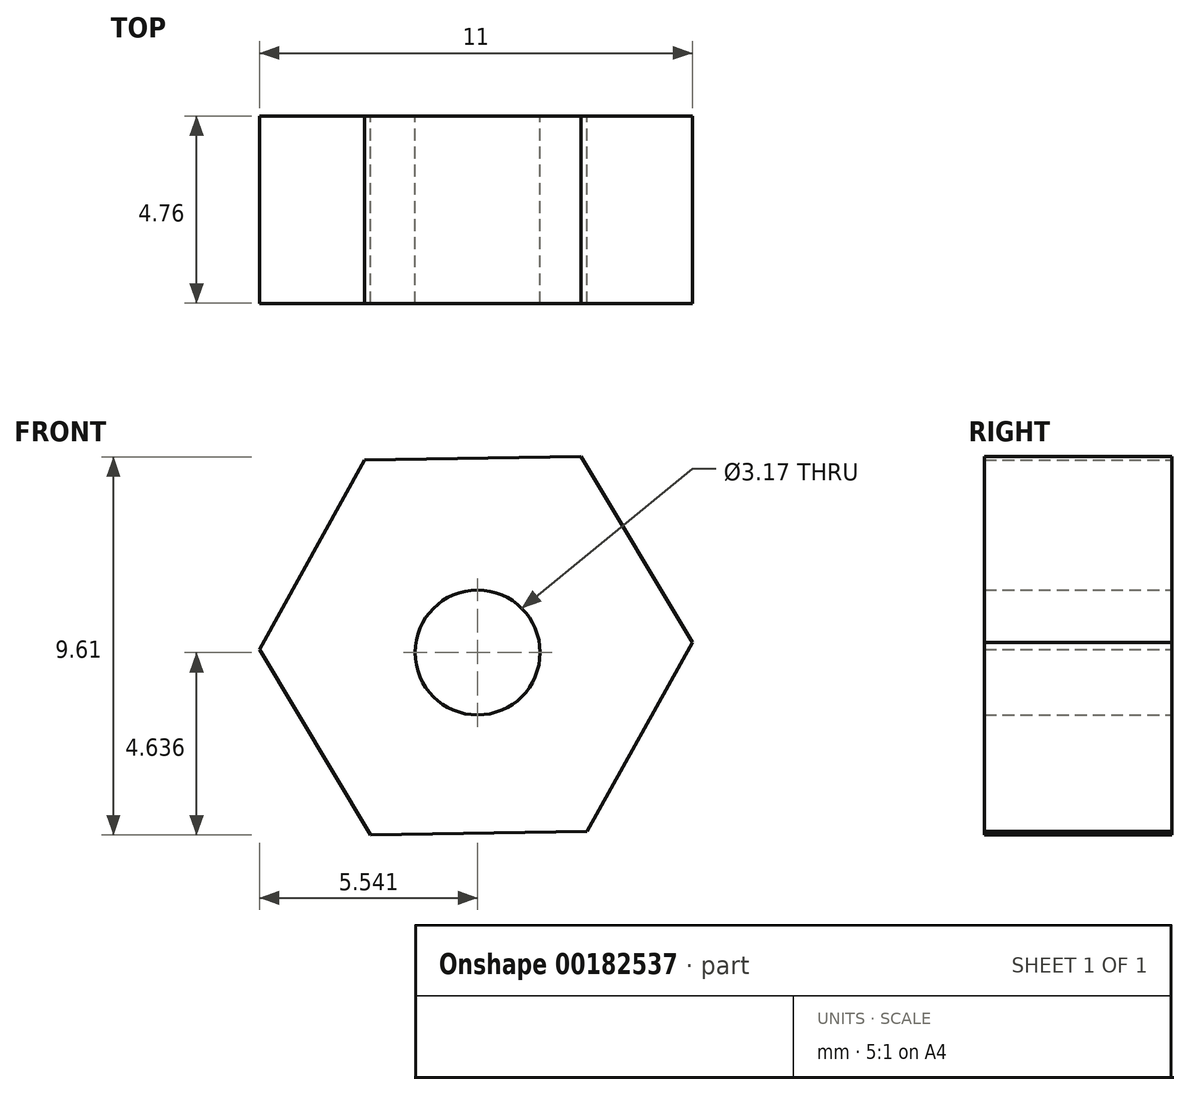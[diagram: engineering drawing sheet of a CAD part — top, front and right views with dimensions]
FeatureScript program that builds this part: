
annotation { "Feature Type Name" : "Feature", "Feature Type Description" : "" }
export const myFeature = defineFeature(function(context is Context, id is Id, definition is map)
    precondition{}
    {
        {
            var Q0;
            Q0=qCreatedBy(makeId("Front.planeOp"),FACE);
            var sketch = newSketch(context, id + "F0", { "sketchPlane" : qUnion([Q0])});
            skCircle(sketch, "E0.cCircle", {"center": v(-7.05, 13.42) * mm, "radius": 4.76 * mm, "construction": true});
            skLineSegment(sketch, "E0.0", {"start": v(-1.55, 13.5) * mm, "end": v(-4.22, 8.7) * mm});
            skLineSegment(sketch, "E0.1", {"start": v(-4.22, 8.7) * mm, "end": v(-9.72, 8.6) * mm});
            skLineSegment(sketch, "E0.2", {"start": v(-9.72, 8.6) * mm, "end": v(-12.55, 13.33) * mm});
            skLineSegment(sketch, "E0.3", {"start": v(-12.55, 13.33) * mm, "end": v(-9.88, 18.13) * mm});
            skLineSegment(sketch, "E0.4", {"start": v(-9.88, 18.13) * mm, "end": v(-4.38, 18.22) * mm});
            skLineSegment(sketch, "E0.5", {"start": v(-4.38, 18.22) * mm, "end": v(-1.55, 13.5) * mm});
            skPoint(sketch, "E0.0.midPoint", {"position": v(-2.89, 11.1) * mm});
            skSolve(sketch);
        }
        {
            var Q0;
            Q0=makeQuery(id+"F0.imprint","IMPRINT",FACE,{"disambiguationData":[TD([[makeQuery(id+"F0.imprint","IMPRINT",EDGE,{"derivedFrom":sQuery(id+"F0.wireOp",EDGE,"E0.0")}),-1.0]])]});
            var sketch = newSketch(context, id + "F1", { "sketchPlane" : qUnion([Q0])});
            skCircle(sketch, "E1", {"center": v(-7, 13.25) * mm, "radius": 1.59 * mm});
            skSolve(sketch);
        }
        {
            var Q0;
            Q0=makeQuery(id+"F0.imprint","IMPRINT",FACE,{"disambiguationData":[TD([[makeQuery(id+"F0.imprint","IMPRINT",EDGE,{"derivedFrom":sQuery(id+"F0.wireOp",EDGE,"E0.0")}),-1.0]])]});
            extrude(context, id + "F2", {"entities" : qUnion([Q0]), "depth" : 4.76 * mm});
        }
        {
            var Q0;
            Q0 = qSketchRegion(id + "F1", true);
            extrude(context, id + "F3", {"entities" : qUnion([Q0]), "operationType" : NewBodyOperationType.REMOVE, "depth" : 4.78 * mm});
        }
    });
